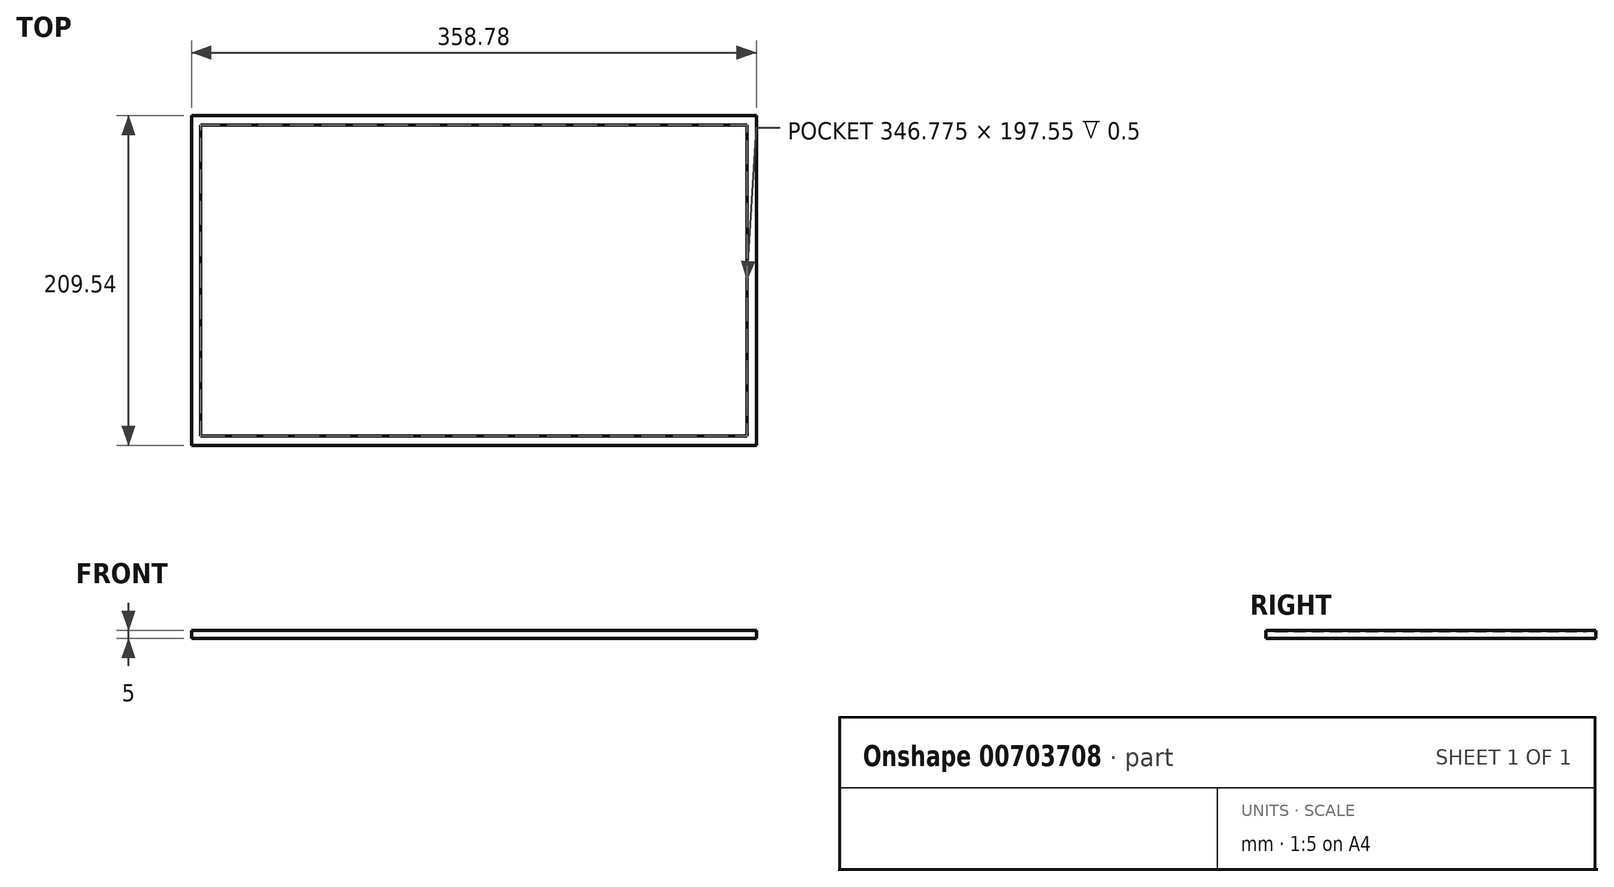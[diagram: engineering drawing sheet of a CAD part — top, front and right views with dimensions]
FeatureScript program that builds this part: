
annotation { "Feature Type Name" : "Feature", "Feature Type Description" : "" }
export const myFeature = defineFeature(function(context is Context, id is Id, definition is map)
    precondition{}
    {
        {
            var Q0;
            Q0=qCreatedBy(makeId("Top.planeOp"),FACE);
            var sketch = newSketch(context, id + "F0", { "sketchPlane" : qUnion([Q0])});
            skLineSegment(sketch, "E0.bottom", {"start": v(179.39, -104.77) * mm, "end": v(-179.39, -104.78) * mm});
            skLineSegment(sketch, "E0.top", {"start": v(179.39, 104.78) * mm, "end": v(-179.39, 104.78) * mm});
            skLineSegment(sketch, "E0.left", {"start": v(179.39, -104.77) * mm, "end": v(179.39, 104.78) * mm});
            skLineSegment(sketch, "E0.right", {"start": v(-179.39, -104.78) * mm, "end": v(-179.39, 104.78) * mm});
            skPoint(sketch, "E0.middle", {"position": v(0, 0) * mm});
            skLineSegment(sketch, "E1.0", {"start": v(173.39, 98.78) * mm, "end": v(-173.39, 98.78) * mm});
            skLineSegment(sketch, "E1.1", {"start": v(173.39, -98.77) * mm, "end": v(173.39, 98.78) * mm});
            skLineSegment(sketch, "E1.2", {"start": v(173.39, -98.77) * mm, "end": v(-173.39, -98.78) * mm});
            skLineSegment(sketch, "E1.3", {"start": v(-173.39, -98.78) * mm, "end": v(-173.39, 98.78) * mm});
            skSolve(sketch);
        }
        {
            var Q0;
            Q0=makeQuery(id+"F0.imprint","IMPRINT",FACE,{"disambiguationData":[TD([[makeQuery(id+"F0.imprint","IMPRINT",EDGE,{"derivedFrom":sQuery(id+"F0.wireOp",EDGE,"E0.bottom")}),-1.0]])]});
            extrude(context, id + "F1", {"entities" : qUnion([Q0]), "depth" : 5 * mm, "offsetDistance" : 25 * mm});
        }
        {
            var Q0;
            Q0=makeQuery(id+"F0.imprint","IMPRINT",FACE,{"disambiguationData":[TD([[makeQuery(id+"F0.imprint","IMPRINT",EDGE,{"derivedFrom":sQuery(id+"F0.wireOp",EDGE,"E1.0")}),1.0]])]});
            extrude(context, id + "F2", {"entities" : qUnion([Q0]), "operationType" : NewBodyOperationType.ADD, "depth" : 4.5 * mm, "offsetDistance" : 25 * mm});
        }
    });
